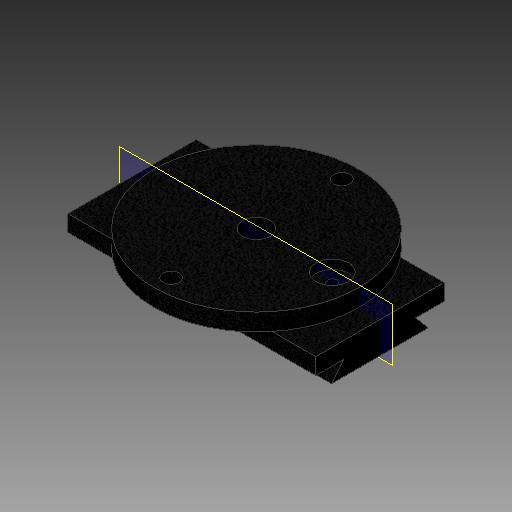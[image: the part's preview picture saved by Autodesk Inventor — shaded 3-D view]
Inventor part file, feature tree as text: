
AUTODESK INVENTOR PART (.ipt)
format: ipt  version: 2018 (Build 220112000, 112)  size: 212,480 bytes
history: native  units: mm
features: extrude x6, sketch x6, plane x1
ambient origin geometry x8: Origin, YZ Plane, XZ Plane, XY Plane, X Axis, Y Axis, Z Axis, Center Point
bodies: Solid1 (feature_tree)
feature tree (13):
  extrude  "Extrusion1"  Depth=19.0mm
  extrude  "Extrusion2"  Depth=165.2mm
  extrude  "Extrusion3"  Depth=11.5mm TaperAngle=0.0deg
  extrude  "Extrusion4"  Depth=73.75mm TaperAngle=0.0deg
  extrude  "Extrusion5"  Depth=6.0mm
  extrude  "Extrusion6"  Depth=5.4mm
  plane  "Work Plane1"
  sketch  "Sketch1"  dims[d1=85.6mm d7=19.0mm]
  sketch  "Sketch3"  dims[d8=165.2mm d9=0.0mm d10=14.0mm]
  sketch  "Sketch4"  dims[d11=68.3mm d12=11.5mm d13=0.0mm]
  sketch  "Sketch5"  dims[d14=18.3mm d15=73.75mm d16=0.0mm]
  sketch  "Sketch7"  dims[d17=6.0mm d18=6.0mm]
  sketch  "Sketch8"  dims[d19=5.4mm d20=5.4mm d21=73.75mm d22=0.0mm d23=6.9mm d24=10.8mm d25=6.0mm d26=0.0mm d27=6.2mm d28=22.8mm d29=0.0mm d30=8.726646mm d31=19.0mm d32=8.726646mm d33=10.0mm]
